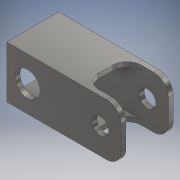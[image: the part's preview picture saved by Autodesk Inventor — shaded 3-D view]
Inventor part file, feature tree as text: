
AUTODESK INVENTOR PART (.ipt)
format: ipt  version: 2018.2 (Build 222227000, 227)  size: 170,496 bytes
history: native  units: mm
features: extrude x5, sketch x5, other x1, fillet x1
ambient origin geometry x8: Origin, YZ Plane, XZ Plane, XY Plane, X Axis, Y Axis, Z Axis, Center Point
bodies: Body1 (feature_tree)
feature tree (12):
  other  "ソリッド1"
  extrude  "押し出し1"  Depth=25.0mm
  extrude  "押し出し2"  Depth=25.0mm
  extrude  "押し出し3"  Depth=55.0mm TaperAngle=0.0deg
  extrude  "押し出し4"  Depth=12.0mm
  extrude  "押し出し5"  Depth=10.0mm
  fillet  "フィレット1"  Radius=12.5mm
  sketch  "スケッチ1"
  sketch  "スケッチ2"
  sketch  "スケッチ3"
  sketch  "スケッチ4"
  sketch  "スケッチ5"
